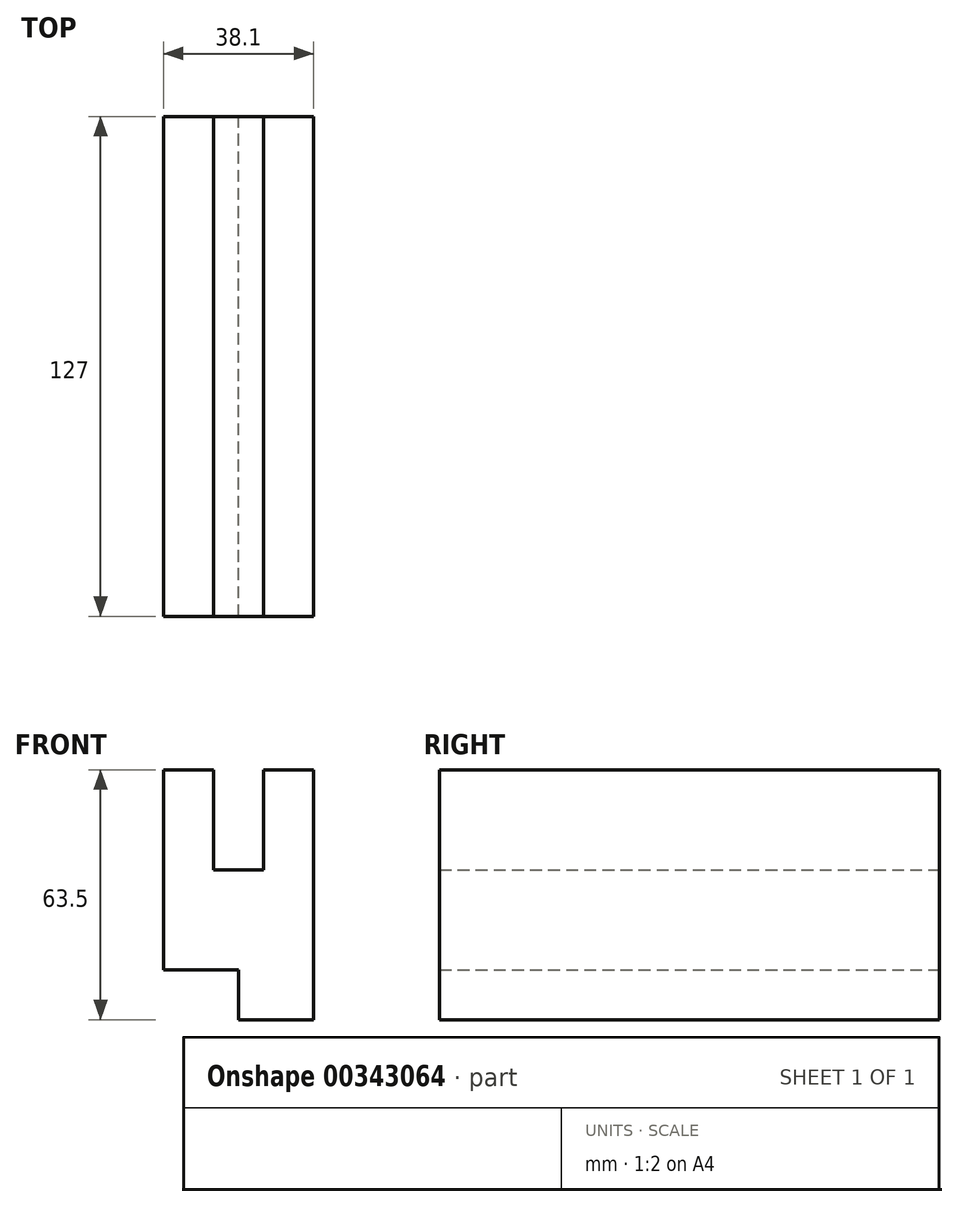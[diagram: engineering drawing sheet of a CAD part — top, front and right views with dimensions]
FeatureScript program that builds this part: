
annotation { "Feature Type Name" : "Feature", "Feature Type Description" : "" }
export const myFeature = defineFeature(function(context is Context, id is Id, definition is map)
    precondition{}
    {
        {
            var Q0;
            Q0=qCreatedBy(makeId("Front.planeOp"),FACE);
            var sketch = newSketch(context, id + "F0", { "sketchPlane" : qUnion([Q0])});
            skLineSegment(sketch, "E0", {"start": v(-47.7, -21.13) * mm, "end": v(-28.65, -21.13) * mm});
            skLineSegment(sketch, "E1", {"start": v(-47.7, -21.13) * mm, "end": v(-47.7, -8.43) * mm});
            skLineSegment(sketch, "E2", {"start": v(-47.7, -8.43) * mm, "end": v(-66.75, -8.43) * mm});
            skLineSegment(sketch, "E3", {"start": v(-28.65, -21.13) * mm, "end": v(-28.65, 42.37) * mm});
            skLineSegment(sketch, "E4", {"start": v(-28.65, 42.37) * mm, "end": v(-41.35, 42.37) * mm});
            skLineSegment(sketch, "E5", {"start": v(-41.35, 42.37) * mm, "end": v(-41.35, 16.97) * mm});
            skLineSegment(sketch, "E6", {"start": v(-41.35, 16.97) * mm, "end": v(-54.05, 16.97) * mm});
            skLineSegment(sketch, "E7", {"start": v(-54.05, 16.97) * mm, "end": v(-54.05, 42.37) * mm});
            skLineSegment(sketch, "E8", {"start": v(-54.05, 42.37) * mm, "end": v(-66.75, 42.37) * mm});
            skLineSegment(sketch, "E9", {"start": v(-66.75, 42.37) * mm, "end": v(-66.75, -8.43) * mm});
            skSolve(sketch);
        }
        {
            var Q0;
            Q0 = qSketchRegion(id + "F0", true);
            extrude(context, id + "F1", {"entities" : qUnion([Q0]), "depth" : 127 * mm});
        }
    });
